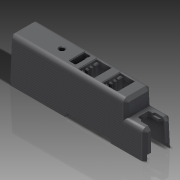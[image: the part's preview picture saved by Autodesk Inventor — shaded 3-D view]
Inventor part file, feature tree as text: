
AUTODESK INVENTOR PART (.ipt)
format: ipt  version: 2011 (Build 150239000, 239)  size: 954,880 bytes
history: native  units: in
note: dims shown in document units (in); Inventor stores cm internally (conversion verified against a paired STEP export)
features: fillet x1, imported_body x1
ambient origin geometry x8: Origin, YZ Plane, XZ Plane, XY Plane, X Axis, Y Axis, Z Axis, Center Point
feature tree (2):
  fillet  "Fillet16"  [1 undecoded]
  imported_body  "Base1"
note: 1 required parameter value undecoded (feature->parameter linkage not recoverable at this tier; creation-order binding heuristic only, values carry confidence <= 0.55)
